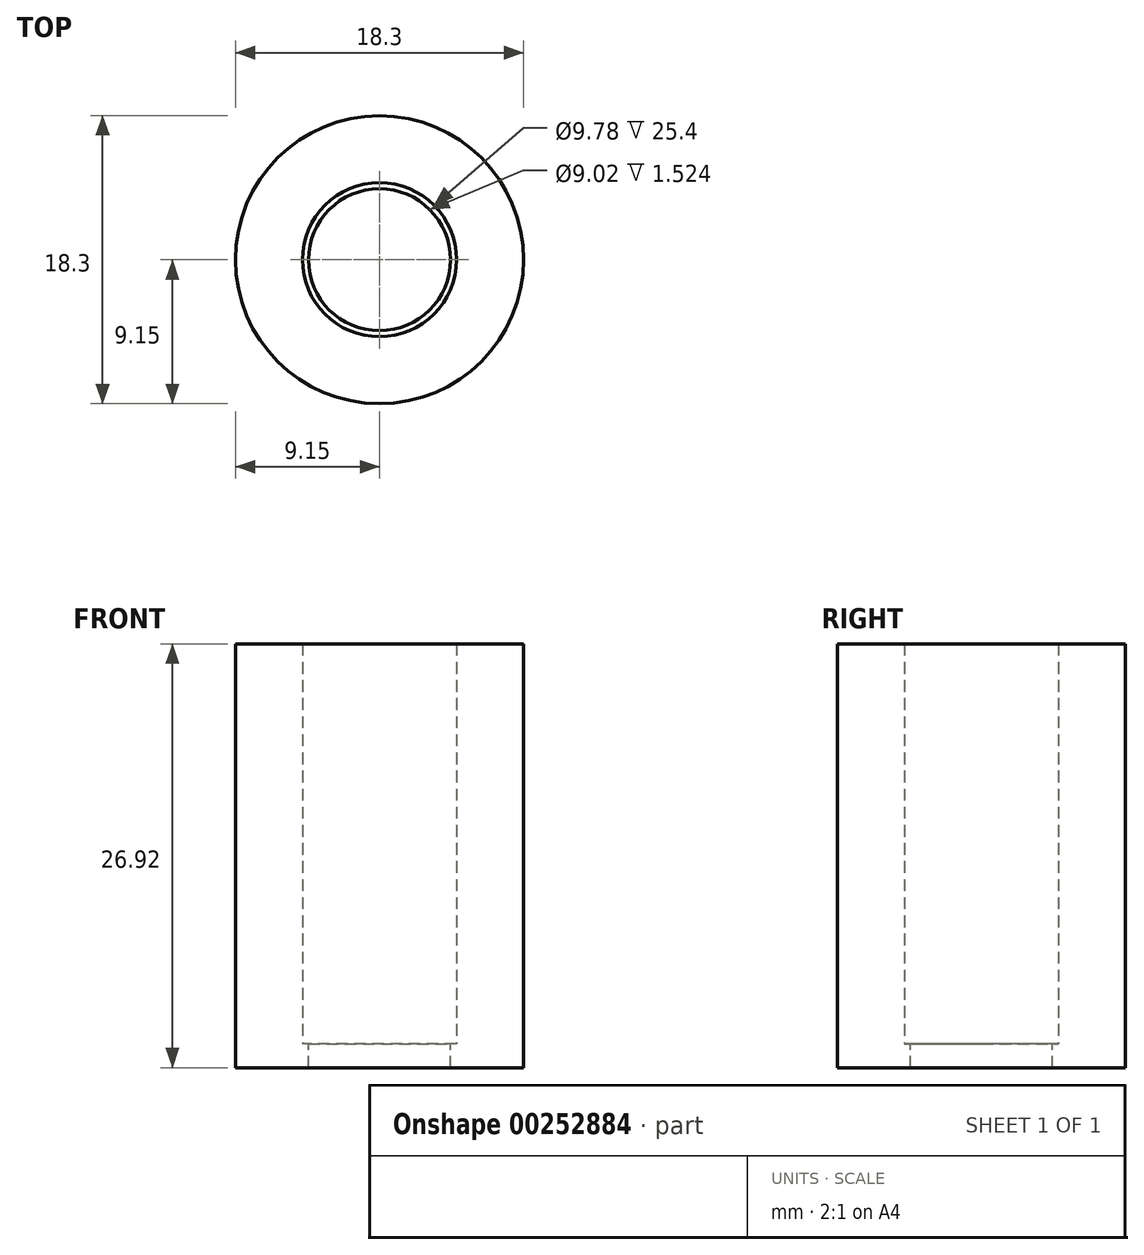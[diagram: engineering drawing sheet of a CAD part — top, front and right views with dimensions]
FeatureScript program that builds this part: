
annotation { "Feature Type Name" : "Feature", "Feature Type Description" : "" }
export const myFeature = defineFeature(function(context is Context, id is Id, definition is map)
    precondition{}
    {
        {
            var Q0;
            Q0=qCreatedBy(makeId("Top.planeOp"),FACE);
            var sketch = newSketch(context, id + "F0", { "sketchPlane" : qUnion([Q0])});
            skCircle(sketch, "E0", {"center": v(0, 0) * mm, "radius": 9.15 * mm});
            skCircle(sketch, "E1", {"center": v(0, 0) * mm, "radius": 4.9 * mm});
            skSolve(sketch);
        }
        {
            var Q0;
            Q0=sQuery(id+"F0.wireOp",EDGE,"E1");
            extrude(context, id + "F1", {"bodyType" : ToolBodyType.SURFACE, "surfaceEntities" : qUnion([Q0]), "depth" : 25.4 * mm});
        }
        {
            var Q0;
            Q0=makeQuery(id+"F0.imprint","IMPRINT",FACE,{"disambiguationData":[TD([[makeQuery(id+"F0.imprint","IMPRINT",EDGE,{"derivedFrom":sQuery(id+"F0.wireOp",EDGE,"E0")}),1.0]])]});
            var Q1;
            Q1=sQuery(id+"F0.wireOp",EDGE,"E0");
            extrude(context, id + "F2", {"entities" : qUnion([Q0]), "surfaceEntities" : qUnion([Q1]), "depth" : 25.4 * mm});
        }
        {
            var Q0;
            Q0=makeQuery(id+"F2.opExtrude","CAP_FACE",FACE,{"disambiguationData":[OSD([sQuery(id+"F0.wireOp",EDGE,"E0"),sQuery(id+"F0.wireOp",EDGE,"E1")])],"isStart":true});
            var sketch = newSketch(context, id + "F3", { "sketchPlane" : qUnion([Q0])});
            skCircle(sketch, "E2.0", {"center": v(0, 0) * mm, "radius": 9.15 * mm});
            skCircle(sketch, "E3", {"center": v(0, 0) * mm, "radius": 4.5 * mm});
            skSolve(sketch);
        }
        {
            var Q0;
            Q0=qSketchRegion(id+"F3",true);
            extrude(context, id + "F4", {"entities" : qUnion([Q0]), "operationType" : NewBodyOperationType.ADD, "depth" : 1.52 * mm});
        }
    });
